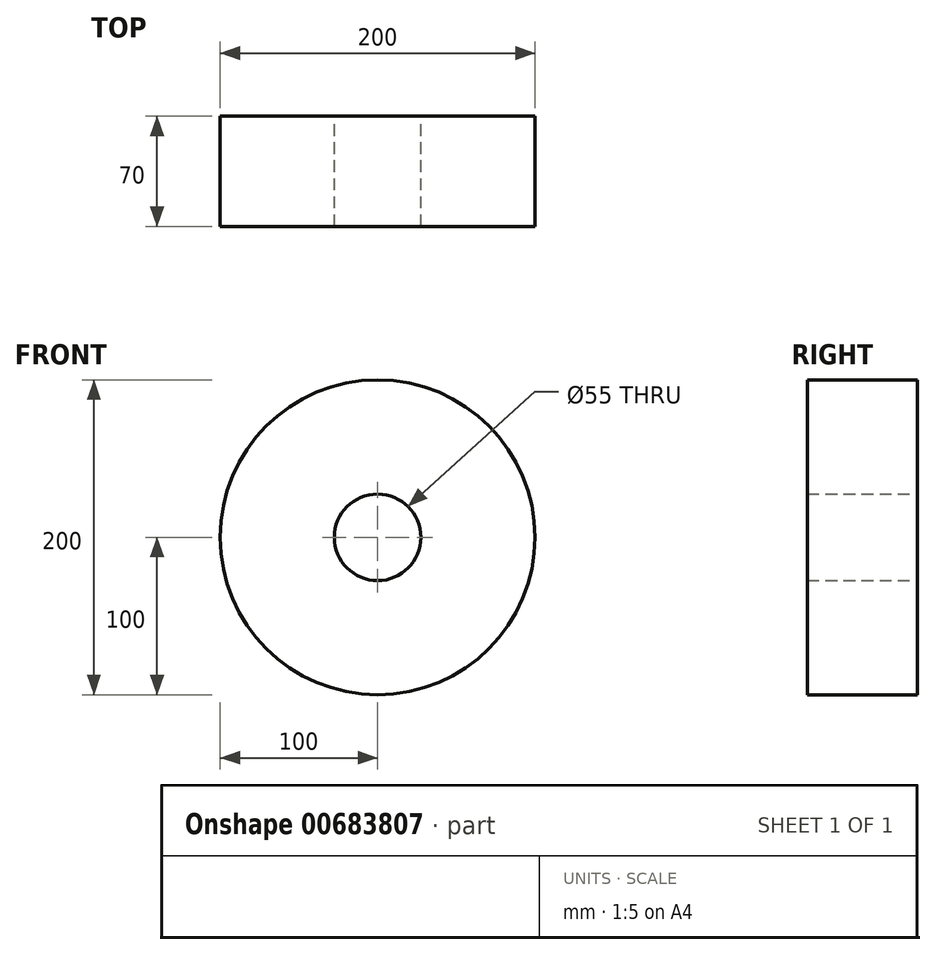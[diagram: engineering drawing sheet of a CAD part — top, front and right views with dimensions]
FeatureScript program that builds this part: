
annotation { "Feature Type Name" : "Feature", "Feature Type Description" : "" }
export const myFeature = defineFeature(function(context is Context, id is Id, definition is map)
    precondition{}
    {
        {
            var Q0;
            Q0=qCreatedBy(makeId("Front.planeOp"),FACE);
            var sketch = newSketch(context, id + "F0", { "sketchPlane" : qUnion([Q0])});
            skCircle(sketch, "E0", {"center": v(0, 0) * mm, "radius": 100 * mm});
            skCircle(sketch, "E1", {"center": v(0, 0) * mm, "radius": 27.5 * mm});
            skPoint(sketch, "E2", {"position": v(0, 76.44) * mm});
            skSolve(sketch);
        }
        {
            var Q0;
            Q0 = qSketchRegion(id + "F0", true);
            extrude(context, id + "F1", {"entities" : qUnion([Q0]), "depth" : 70 * mm, "offsetDistance" : 25 * mm});
        }
    });
